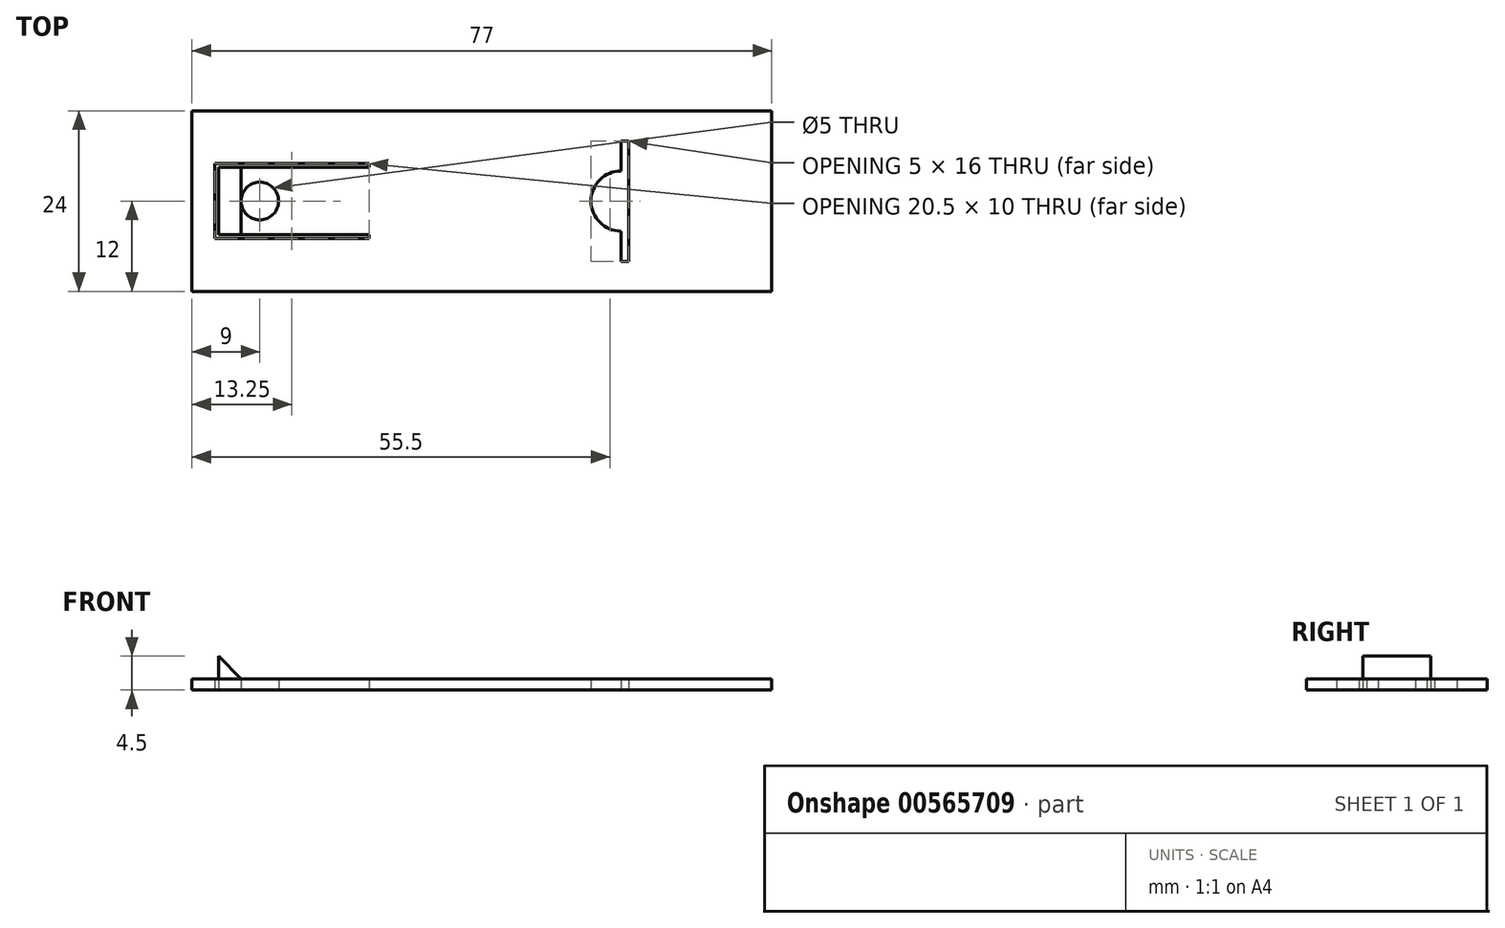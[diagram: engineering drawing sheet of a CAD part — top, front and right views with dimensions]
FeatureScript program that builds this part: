
annotation { "Feature Type Name" : "Feature", "Feature Type Description" : "" }
export const myFeature = defineFeature(function(context is Context, id is Id, definition is map)
    precondition{}
    {
        {
            var Q0;
            Q0=qCreatedBy(makeId("Top.planeOp"),FACE);
            var sketch = newSketch(context, id + "F0", { "sketchPlane" : qUnion([Q0])});
            skLineSegment(sketch, "E0.bottom", {"start": v(-38.5, 12) * mm, "end": v(38.5, 12) * mm});
            skLineSegment(sketch, "E0.top", {"start": v(-38.5, -12) * mm, "end": v(38.5, -12) * mm});
            skLineSegment(sketch, "E0.left", {"start": v(-38.5, 12) * mm, "end": v(-38.5, -12) * mm});
            skLineSegment(sketch, "E0.right", {"start": v(38.5, 12) * mm, "end": v(38.5, -12) * mm});
            skPoint(sketch, "E0.middle", {"position": v(0, 0) * mm});
            skLineSegment(sketch, "E1.bottom", {"start": v(-35.5, 5) * mm, "end": v(-15, 5) * mm});
            skLineSegment(sketch, "E1.top", {"start": v(-35.5, -5) * mm, "end": v(-15, -5) * mm});
            skLineSegment(sketch, "E1.left", {"start": v(-35.5, 5) * mm, "end": v(-35.5, -5) * mm});
            skLineSegment(sketch, "E1.right", {"start": v(-15, 5) * mm, "end": v(-15, 4.5) * mm});
            skPoint(sketch, "E1.middle", {"position": v(-25.25, 0) * mm});
            skLineSegment(sketch, "E2.bottom", {"start": v(-15, -4.5) * mm, "end": v(-35, -4.5) * mm});
            skLineSegment(sketch, "E2.top", {"start": v(-15, 4.5) * mm, "end": v(-35, 4.5) * mm});
            skLineSegment(sketch, "E2.right", {"start": v(-35, -4.5) * mm, "end": v(-35, 4.5) * mm});
            skPoint(sketch, "E2.middle", {"position": v(-25, 0) * mm});
            skLineSegment(sketch, "E3.bottom", {"start": v(18.5, 8) * mm, "end": v(19.5, 8) * mm});
            skLineSegment(sketch, "E3.top", {"start": v(18.5, -8) * mm, "end": v(19.5, -8) * mm});
            skLineSegment(sketch, "E3.left", {"start": v(18.5, 8) * mm, "end": v(18.5, 4) * mm});
            skLineSegment(sketch, "E3.right", {"start": v(19.5, 8) * mm, "end": v(19.5, -8) * mm});
            skPoint(sketch, "E3.middle", {"position": v(19, 0) * mm});
            skArc(sketch, "E4", {"start": v(18.5, 4) * mm, "mid": v(14.5, 0) * mm, "end": v(18.5, -4) * mm});
            skLineSegment(sketch, "E5.trimOffspring", {"start": v(18.5, -4) * mm, "end": v(18.5, -8) * mm});
            skCircle(sketch, "E6", {"center": v(-29.5, 0) * mm, "radius": 2.5 * mm});
            skLineSegment(sketch, "E7.trimOffspring", {"start": v(-15, -4.5) * mm, "end": v(-15, -5) * mm});
            skSolve(sketch);
        }
        {
            var Q0;
            Q0 = qSketchRegion(id + "F0", true);
            extrude(context, id + "F1", {"entities" : qUnion([Q0]), "depth" : 1.5 * mm, "offsetDistance" : 25 * mm});
        }
        {
            var Q0;
            Q0=makeQuery(id+"F1.opExtrude","CAP_FACE",FACE,{"disambiguationData":[OSD([sQuery(id+"F0.wireOp",EDGE,"E0.bottom"),sQuery(id+"F0.wireOp",EDGE,"E0.top"),sQuery(id+"F0.wireOp",EDGE,"E0.left"),sQuery(id+"F0.wireOp",EDGE,"E0.right"),sQuery(id+"F0.wireOp",EDGE,"E1.bottom"),sQuery(id+"F0.wireOp",EDGE,"E1.top"),sQuery(id+"F0.wireOp",EDGE,"E1.left"),sQuery(id+"F0.wireOp",EDGE,"E1.right"),sQuery(id+"F0.wireOp",EDGE,"E2.bottom"),sQuery(id+"F0.wireOp",EDGE,"E2.top"),sQuery(id+"F0.wireOp",EDGE,"E2.right"),sQuery(id+"F0.wireOp",EDGE,"E3.bottom"),sQuery(id+"F0.wireOp",EDGE,"E3.top"),sQuery(id+"F0.wireOp",EDGE,"E3.left"),sQuery(id+"F0.wireOp",EDGE,"E3.right"),sQuery(id+"F0.wireOp",EDGE,"E4"),sQuery(id+"F0.wireOp",EDGE,"E5.trimOffspring"),sQuery(id+"F0.wireOp",EDGE,"E6"),sQuery(id+"F0.wireOp",EDGE,"E7.trimOffspring")])],"isStart":false});
            var sketch = newSketch(context, id + "F2", { "sketchPlane" : qUnion([Q0])});
            skLineSegment(sketch, "E8.bottom", {"start": v(-35, 4.5) * mm, "end": v(-32, 4.5) * mm});
            skLineSegment(sketch, "E8.top", {"start": v(-35, -4.5) * mm, "end": v(-32, -4.5) * mm});
            skLineSegment(sketch, "E8.left", {"start": v(-35, 4.5) * mm, "end": v(-35, -4.5) * mm});
            skLineSegment(sketch, "E8.right", {"start": v(-32, 4.5) * mm, "end": v(-32, -4.5) * mm});
            skSolve(sketch);
        }
        {
            var Q0;
            Q0 = qSketchRegion(id + "F2", true);
            extrude(context, id + "F3", {"entities" : qUnion([Q0]), "operationType" : NewBodyOperationType.ADD, "depth" : 3 * mm, "offsetDistance" : 25 * mm});
        }
        {
            var Q0;
            Q0=makeQuery(id+"F3.opExtrude","CAP_EDGE",EDGE,{"disambiguationData":[OSD([sQuery(id+"F2.wireOp",EDGE,"E8.right")])],"isStart":false});
            chamfer(context, id + "F4", {"entities" : qUnion([Q0]), "width" : 3 * mm, "tangentPropagation" : true});
        }
    });
